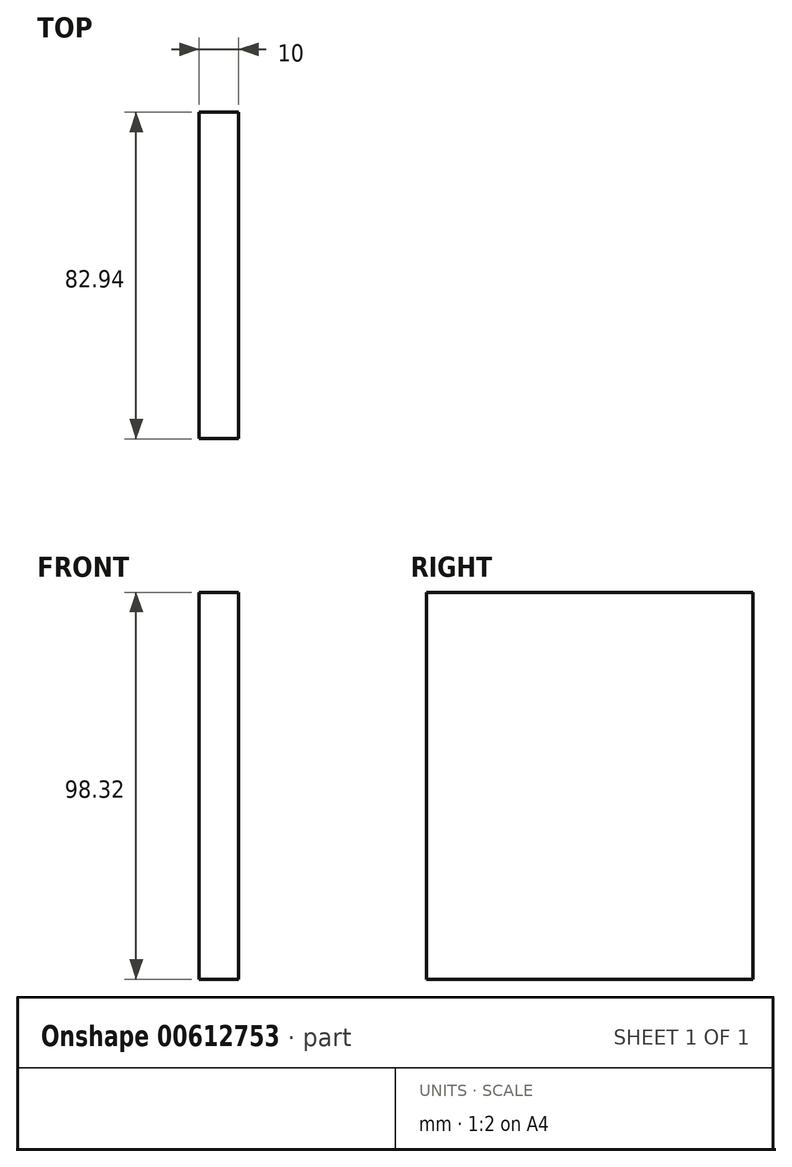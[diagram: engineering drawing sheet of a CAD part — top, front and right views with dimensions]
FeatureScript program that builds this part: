
annotation { "Feature Type Name" : "Feature", "Feature Type Description" : "" }
export const myFeature = defineFeature(function(context is Context, id is Id, definition is map)
    precondition{}
    {
        {
            var Q0;
            Q0=qCreatedBy(makeId("Right.planeOp"),FACE);
            var sketch = newSketch(context, id + "F0", { "sketchPlane" : qUnion([Q0])});
            skLineSegment(sketch, "E0.bottom", {"start": v(-41.47, 49.16) * mm, "end": v(41.47, 49.16) * mm});
            skLineSegment(sketch, "E0.top", {"start": v(-41.47, -49.16) * mm, "end": v(41.47, -49.16) * mm});
            skLineSegment(sketch, "E0.left", {"start": v(-41.47, 49.16) * mm, "end": v(-41.47, -49.16) * mm});
            skLineSegment(sketch, "E0.right", {"start": v(41.47, 49.16) * mm, "end": v(41.47, -49.16) * mm});
            skPoint(sketch, "E1", {"position": v(0, 49.16) * mm});
            skPoint(sketch, "E2", {"position": v(41.47, 0) * mm});
            skSolve(sketch);
        }
        {
            var Q0;
            Q0=makeQuery(id+"F0.imprint","IMPRINT",FACE,{"disambiguationData":[TD([[makeQuery(id+"F0.imprint","IMPRINT",EDGE,{"derivedFrom":sQuery(id+"F0.wireOp",EDGE,"E0.bottom")}),-1.0]])]});
            extrude(context, id + "F1", {"entities" : qUnion([Q0]), "depth" : 10 * mm, "offsetDistance" : 25 * mm});
        }
        {
            var Q0;
            Q0=makeQuery(id+"F1.opExtrude","CAP_FACE",FACE,{"disambiguationData":[OSD([sQuery(id+"F0.wireOp",EDGE,"E0.bottom"),sQuery(id+"F0.wireOp",EDGE,"E0.top"),sQuery(id+"F0.wireOp",EDGE,"E0.left"),sQuery(id+"F0.wireOp",EDGE,"E0.right")])],"isStart":false});
            var sketch = newSketch(context, id + "F2", { "sketchPlane" : qUnion([Q0])});
            skCircle(sketch, "E3", {"center": v(0, 39.16) * mm, "radius": 2.4 * mm});
            skSolve(sketch);
        }
    });
